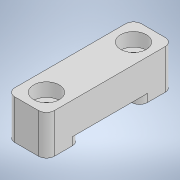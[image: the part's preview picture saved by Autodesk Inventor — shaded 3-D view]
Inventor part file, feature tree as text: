
AUTODESK INVENTOR PART (.ipt)
format: ipt  version: 2022 (Build 260153000, 153)  size: 140,288 bytes
history: native  units: mm
features: sketch x3, extrude x2, fillet x2, hole x1
ambient origin geometry x8: Origin, YZ Plane, XZ Plane, XY Plane, X Axis, Y Axis, Z Axis, Center Point
bodies: Solid1 (feature_tree)
feature tree (8):
  extrude  "Extrusion1"  Depth=10.0mm
  hole  "Hole1"  [1 undecoded]
  fillet  "Fillet1"  Radius=2.0mm
  extrude  "Extrusion2"  Depth=15.0mm
  fillet  "Fillet2"  Radius=2.0mm
  sketch  "Sketch1"  dims[d0=32.0mm d1=10.0mm]
  sketch  "Sketch2"  dims[d2=10.0mm d3=0.0mm d4=22.0mm]
  sketch  "Sketch3"  dims[d5=3.4mm d6=6.0mm d7=6.5mm d8=3.4mm d9=14.3117mm d10=8.0mm d11=20.594885mm d12=2.0mm d13=15.0mm d14=2.0mm d15=0.0mm d16=0.0mm d17=2.0mm]
note: 1 required parameter value undecoded (feature->parameter linkage not recoverable at this tier; creation-order binding heuristic only, values carry confidence <= 0.55)
